# Revit family: PRD_FrankeWS_ShwrMxrs_SelfClosingShowerValve_F3SV2003
name_source: partatom
category: Plumbing Fixtures
revit_build: Autodesk Revit 2018 (Build: 20190510_1515(x64)
units: mm (PartAtom-declared; Revit-internal decimal feet)

## family parameters
Cut with Voids When Loaded = Yes
Host = Face
OmniClass Number = 23.45.05.14.99
OmniClass Title = Other Sanitary Washing Plumbing Fixtures
Part Type = Normal
Room Calculation Point = No
Round Connector Dimension = Use Diameter
Shared = No

## types (1)
- F3SV2003 - 0.20 L/s
    AdditionalConnections = no
    AdjustableFlowTime = yes
    AssetType = Fixed
    BIMObjectName = PRD_AR_ShwrMxrs_SelfClosingShowerValve_F3SV2003
    Category = Pr_40_20_87_78, Shower manual water supply sets
    Circulation = no
    CloseOffRating = 0.0 Pa
    Color = Chrome
    ConnectionWithPayWaterDispenser = not possible
    Default Elevation = 850 mm  [stored 2.78871 ft]
    Description = F3S self-closing straight-way valve DN 15 for in-wall mounting with noise-reducing styrene cladding, for shower facilities. Self-closing functional part, hydraulically controlled, piston-free design, self-closing, stepless adjustment of flow duration. For connection to pre-mixed hot water or cold water. Casing including changeable valve seat, with internal thread G 1/2, visible parts high-polished, chromium-plated brass. With rosette, depth adjustability 15 mm.
    DiameterNominal = 15.000 mm
    DurationUnit = year
    Features = For connection to pre-mixed hot water or cold water, high-polished chromium-plated brass.
    Finish = high-polished chromium-plated brass
    FlowCoefficient = 0
    FlowColdWater = 0.2 L/s
    FunctionalPrinciple = hydraulic self-closing
    GrossWeight = 0.65 kg
    HygieneFlushing = no
    IfcExportAs = IfcValveType
    IfcExportType = COMMON
    InletSize = G-1-2
    Manufacturer = KWC Group AG
    ManufacturerName = KWC Group AG
    ManufacturerURL = www.kwc.com
    Material = Brass
    MaterialsBody = Brass
    MaximumFlowTime = 35.00 seconds
    MinimumFlowPressure = 1.00 bar
    MinimumFlowTime = 5.00 seconds
    Model = F3SV2003
    ModelNumber = 2030034416
    ModelReference = F3SV2003
    NBSDescription = Shower manual water supply sets
    NBSReference = 45-35-70/335
    Name = F3 self-closing shower valve F3SV2003
    NetWeight = 0.60 kg
    NominalHeight = 0 mm  [stored 0 ft]
    NominalLength = 0 mm  [stored 0 ft]
    NominalWidth = 0 mm  [stored 0 ft]
    PositionOfWaterConnection = from bottom
    ProductInformation = https://pim.kwc.com
    ProtectiveShutdown = no
    RingMaterial = PRD_AR_SyntheticDarkRed
    ShowerPipeDraining = no
    SoundInsulation = no
    TapMaterial = PRD_AR_ChromatedBrass_HighPolished
    TestPressure = 0.0 Pa
    ThermalDisinfection = no
    TypeOfMixing = no mixing
    TypeOfMounting = in-wall installation without box
    TypeOfOperation = manual operation
    TypeOfShower = in-wall fitting
    URL = www.kwc.com
    Uniclass2015Code = Pr_40_20_87_78
    Uniclass2015Title = Shower manual water supply sets
    Uniclass2015Version = Products v1.10
    ValveMechanism = Other
    ValveOperation = Other
    ValvePattern = STRAIGHT_2_PORT
    Version = 1
    VolumeFlowRate = 0.20 L/s at 3 bar
    WarrantyDurationUnit = year

note: [stored X ft] marks values corroborated as IEEE doubles in the binary element streams (Revit-internal decimal feet)

## geometry (parser evidence)
native form markers: Sweep x2
no freeform markers — native parametric forms only
